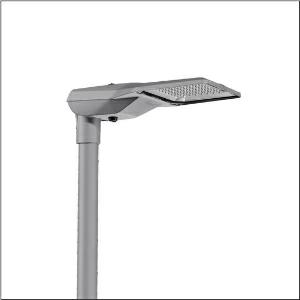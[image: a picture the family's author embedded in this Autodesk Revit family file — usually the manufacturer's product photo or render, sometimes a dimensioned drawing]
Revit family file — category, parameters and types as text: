
# Revit family: streetlight_sl_21_iq_midi___st0_8a_5xe3c31y08nb_292d
name_source: partatom
category: Lighting Fixtures
units: mm (PartAtom-declared; Revit-internal decimal feet)

## family parameters
Cut with Voids When Loaded = No
Host = Face
Light Source = No
Part Type = Normal
Room Calculation Point = No
Round Connector Dimension = Use Diameter
Shared = No

## types (1)
- --- (1 x LED, 21550 lm, 136.6 W, 3000K)
    Apparent Load = 137 VA
    CIE Flux Codes = 41 75 97 100 100
    Color Rendering = 70
    Color Temperature = 3000K
    Default Elevation = 1800 mm
    Description = Streetlight SL 21 iQ midi, mast luminaire, primary light control with lens, of PMMA, primary optical cover: cover, of toughened safety glass, transparent, light distribution: ST0.8a, light emission: direct distribution, primary light characteristic: asymmetric, installation type: post-top, side-entry, LED, High Power LED, rated luminous flux: 21.550lm, luminous efficacy: 158lm/W, light colour: 730, colour temperature: 3000K, control: pre-setting: logarithmic dimming characteristic, Street-Remote, Auto-Match, Temp-Guard, Lumen-Switch, Night-Set, Smart-Wire, Light-Fading, Desk-Remote (wireless, voltage-free reading and setting of iQ features in the workshop via application-optimized NFC function/RFID function), optimised constant luminous flux control (CLO 2.0), mains connection: 230..240V, AC, 50/60Hz, start of lifetime: 137W, end of service life: 144W, reduction: 61W, luminaire housing, of diecast aluminium, powder-coated, Siteco® metallic grey (DB 702S), corrosivity category C5 mid according to DIN EN ISO 12944, please order mast flange separately, inclination adjustable: 0°, 5°, 10°, 15°, sealing non-destructively replaceable, multi-level sealing system, length: 644mm, width: 335mm, height: 110mm, mast flange for spigot size: 42mm (side-entry): 5XC10008XM4, 60/48mm (side-entry/post-top): 5XC10108XM2, 76/60mm (side-entry/post-top): 5XC10108XM1, Smart Interface below and above, protection rating (complete): IP66, insulation class (complete): insulation class II (safety insulation), certification: CE, ENEC, ENEC+, VDE, impact resistance: IK09, permissible operating ambient temperature for outdoor applications: -40..+50°C, standard-compliant lighting for roads and squares, packaging unit: 1 piece

Light Distribution: ST0.8a
    Height = 111 mm
    Lamp = 1 x LED
    Lamp Light Flux = 21550 lm
    Lamp Power = 136.6 W
    Lamp count = 1
    Length = 644 mm
    Luminous efficacy = 158 lm/W
    Manufacturer = Siteco
    ModVariant = No
    Model = 5XE3C31Y08NB
    Number of Poles = 1
    OnlyDefault = Yes
    Power Factor = 1
    Product Name = Streetlight SL 21 iQ midi | ST0.8a
    Product group = mast luminaire | pylon top
    ProductGroupID = 6100
    Protection Class = Protection class II
    Protection Degree = IP 66
    RLX_Detail_Level = 1
    RLX_Emergency_Light_Flux = 0 lm
    RLX_Emergency_Type = 0
    RLX_Emergency_Type_DB = No
    RlxData = <blob elided: 91073 chars, md5=205195cf>
    Socket = socket
    Standby Power = 0 W
    System Light Flux = 21550 lm
    System Power = 137 W
    Type Comments = factory setting: luminous flux: 100 % | dim-lin: 254 | 733 mA
    Type Image = l_1004304.jpg
    URL = http://relux.com
    VarID = @adj_082041
    Voltage = 0 V
    Weight = 0.00 kg
    Width = 336 mm

## geometry (parser evidence)
native form markers: Blend x4, Sweep x10
no freeform markers — native parametric forms only
